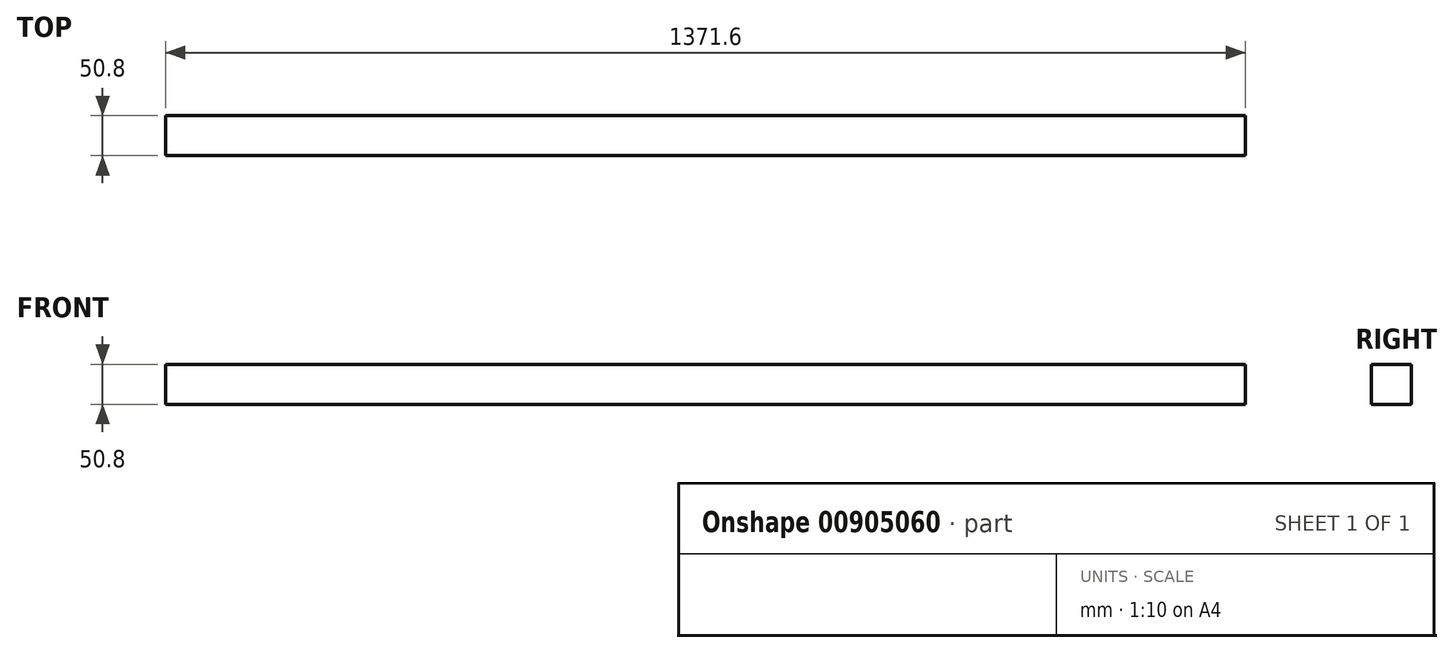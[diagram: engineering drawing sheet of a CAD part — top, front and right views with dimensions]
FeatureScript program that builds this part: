
annotation { "Feature Type Name" : "Feature", "Feature Type Description" : "" }
export const myFeature = defineFeature(function(context is Context, id is Id, definition is map)
    precondition{}
    {
        {
            var Q0;
            Q0=qCreatedBy(makeId("Top.planeOp"),FACE);
            var sketch = newSketch(context, id + "F0", { "sketchPlane" : qUnion([Q0])});
            skLineSegment(sketch, "E0.bottom", {"start": v(685.8, 25.4) * mm, "end": v(-685.8, 25.4) * mm});
            skLineSegment(sketch, "E0.top", {"start": v(685.8, -25.4) * mm, "end": v(-685.8, -25.4) * mm});
            skLineSegment(sketch, "E0.left", {"start": v(685.8, 25.4) * mm, "end": v(685.8, -25.4) * mm});
            skLineSegment(sketch, "E0.right", {"start": v(-685.8, 25.4) * mm, "end": v(-685.8, -25.4) * mm});
            skPoint(sketch, "E0.middle", {"position": v(0, 0) * mm});
            skSolve(sketch);
        }
        {
            var Q0;
            Q0 = qSketchRegion(id + "F0", true);
            extrude(context, id + "F1", {"entities" : qUnion([Q0]), "depth" : 50.8 * mm, "offsetDistance" : 25.4 * mm});
        }
    });
